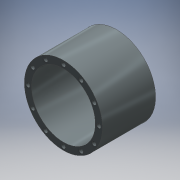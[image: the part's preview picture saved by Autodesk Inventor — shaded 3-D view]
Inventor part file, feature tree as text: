
AUTODESK INVENTOR PART (.ipt)
format: ipt  version: 2016 (Build 200138000, 138)  size: 139,776 bytes
history: native  units: mm
features: extrude x2, sketch x2
ambient origin geometry x8: Origin, YZ Plane, XZ Plane, XY Plane, X Axis, Y Axis, Z Axis, Center Point
bodies: Solid1 (feature_tree)
feature tree (4):
  extrude  "Extrusion1"  Depth=44.0mm
  extrude  "Extrusion2"  Depth=30.0mm
  sketch  "Sketch1"  dims[d0=36.0mm d1=44.0mm]
  sketch  "Sketch2"  dims[d2=30.0mm d3=0.0mm d4=2.35mm d5=0.0mm d6=20.0mm d7=120.0mm d9=360.0deg d11=0.0mm d12=0.0mm]
